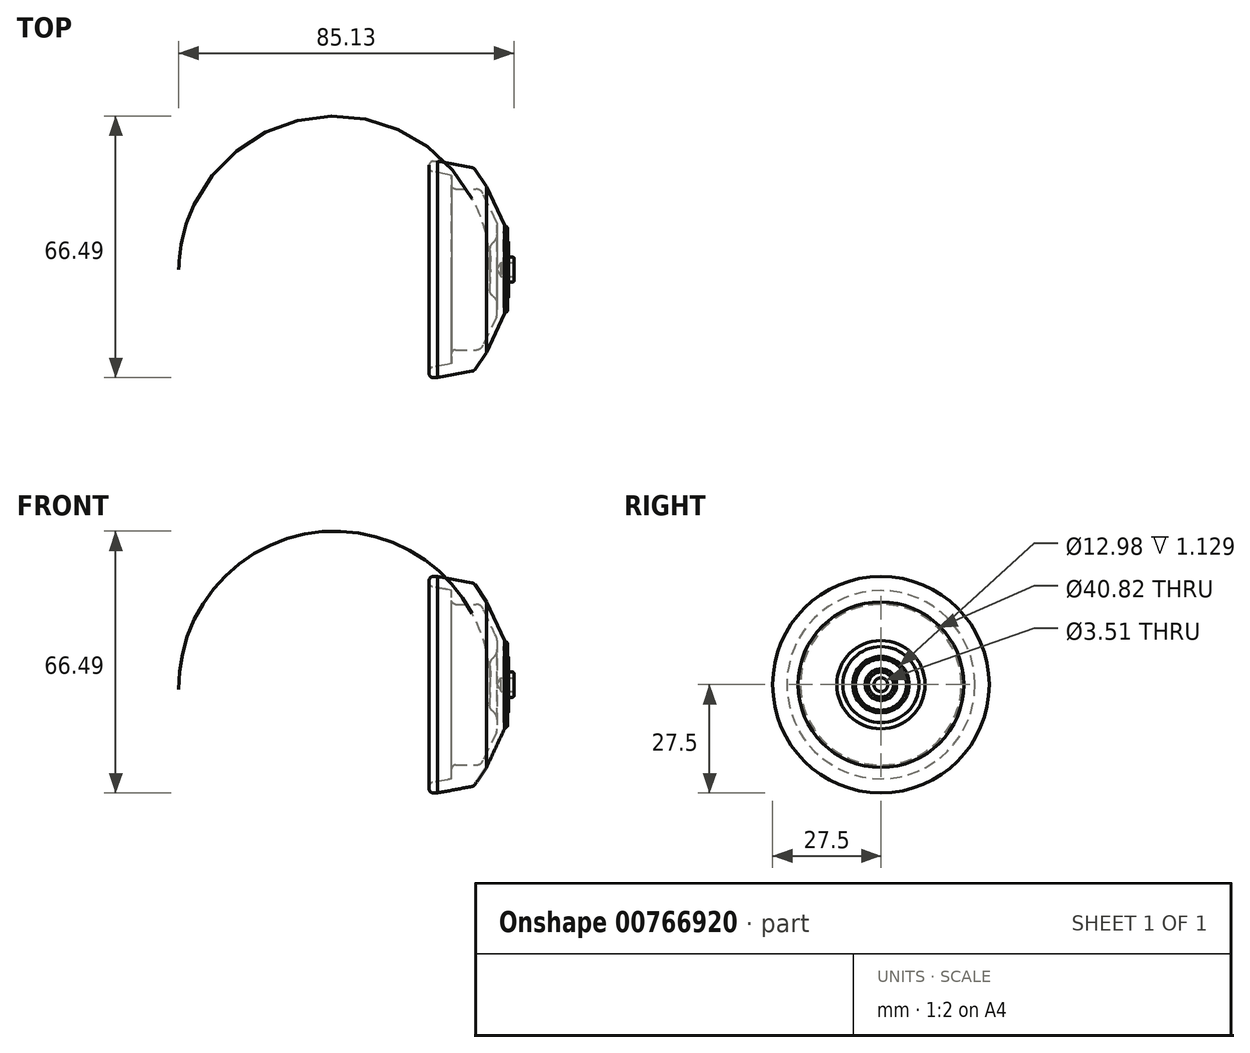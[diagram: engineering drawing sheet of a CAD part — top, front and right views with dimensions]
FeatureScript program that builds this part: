
annotation { "Feature Type Name" : "Feature", "Feature Type Description" : "" }
export const myFeature = defineFeature(function(context is Context, id is Id, definition is map)
    precondition{}
    {
        {
            var Q0;
            Q0=qCreatedBy(makeId("Front.planeOp"),FACE);
            var sketch = newSketch(context, id + "F0", { "sketchPlane" : qUnion([Q0])});
            skLineSegment(sketch, "E0", {"start": v(4.25, 1.75) * mm, "end": v(1.05, 1.75) * mm});
            skArc(sketch, "E1", {"start": v(2.42, 9.65) * mm, "mid": v(2.6, 9.73) * mm, "end": v(2.67, 9.9) * mm});
            skLineSegment(sketch, "E2", {"start": v(1.67, 7.15) * mm, "end": v(1.67, 9.65) * mm});
            skLineSegment(sketch, "E3", {"start": v(1.67, 9.65) * mm, "end": v(2.42, 9.65) * mm});
            skLineSegment(sketch, "E4", {"start": v(2.93, 6.62) * mm, "end": v(2.93, 6.9) * mm});
            skLineSegment(sketch, "E5", {"start": v(1.05, 1.75) * mm, "end": v(0, 0) * mm});
            skArc(sketch, "E6", {"start": v(2.93, 6.9) * mm, "mid": v(2.85, 7.08) * mm, "end": v(2.67, 7.15) * mm});
            skArc(sketch, "E7", {"start": v(2.8, 6.5) * mm, "mid": v(2.9, 6.53) * mm, "end": v(2.93, 6.62) * mm});
            skLineSegment(sketch, "E8", {"start": v(1.67, 6.5) * mm, "end": v(2.8, 6.5) * mm});
            skLineSegment(sketch, "E9", {"start": v(1.67, 4) * mm, "end": v(1.67, 6.5) * mm});
            skLineSegment(sketch, "E10", {"start": v(1.67, 4) * mm, "end": v(2.37, 4) * mm});
            skLineSegment(sketch, "E11", {"start": v(4.25, 1.75) * mm, "end": v(4.25, 2.97) * mm});
            skLineSegment(sketch, "E12", {"start": v(2.37, 3.19) * mm, "end": v(2.37, 4) * mm});
            skLineSegment(sketch, "E13", {"start": v(4.16, 3.09) * mm, "end": v(3.88, 3.18) * mm});
            skLineSegment(sketch, "E14", {"start": v(2.37, 3.19) * mm, "end": v(3.84, 3.19) * mm});
            skLineSegment(sketch, "E15", {"start": v(1.67, 7.15) * mm, "end": v(2.67, 7.15) * mm});
            skArc(sketch, "E16", {"start": v(4.25, 2.97) * mm, "mid": v(4.22, 3.04) * mm, "end": v(4.16, 3.09) * mm});
            skArc(sketch, "E17", {"start": v(3.88, 3.18) * mm, "mid": v(3.86, 3.18) * mm, "end": v(3.84, 3.19) * mm});
            skLineSegment(sketch, "E18", {"start": v(4.75, 1) * mm, "end": v(4.75, 2.5) * mm});
            skPoint(sketch, "E19.orphan", {"position": v(4.75, 0) * mm});
            skPoint(sketch, "E20.end.orphan", {"position": v(-17.25, -3.5) * mm});
            skPoint(sketch, "E20.start.orphan", {"position": v(4.75, -3.5) * mm});
            skLineSegment(sketch, "E21", {"start": v(-17.25, 27.5) * mm, "end": v(-15.16, 27.5) * mm});
            skLineSegment(sketch, "E22", {"start": v(2.67, 9.9) * mm, "end": v(2.67, 10.56) * mm});
            skLineSegment(sketch, "E23", {"start": v(2.67, 10.56) * mm, "end": v(1.87, 11.22) * mm});
            skLineSegment(sketch, "E24", {"start": v(1.87, 11.22) * mm, "end": v(-2.73, 21.05) * mm});
            skLineSegment(sketch, "E25", {"start": v(-2.73, 21.05) * mm, "end": v(-5.9, 25.79) * mm});
            skLineSegment(sketch, "E26", {"start": v(-5.9, 25.79) * mm, "end": v(-15.16, 27.5) * mm});
            skPoint(sketch, "E27.start.orphan", {"position": v(-17.25, 0) * mm});
            skLineSegment(sketch, "E28.0", {"start": v(0, 11.68) * mm, "end": v(-4.1, 20.4) * mm});
            skPoint(sketch, "E29.endSnap0", {"position": v(-10.53, 26.64) * mm});
            skLineSegment(sketch, "E30", {"start": v(-10.53, 20.4) * mm, "end": v(-4.1, 20.4) * mm});
            skPoint(sketch, "E31.orphan", {"position": v(-6.18, 24.31) * mm});
            skLineSegment(sketch, "E32", {"start": v(-17.25, 26.03) * mm, "end": v(-17.25, 27.5) * mm});
            skLineSegment(sketch, "E33", {"start": v(0, 0) * mm, "end": v(-1.64, 0) * mm});
            skLineSegment(sketch, "E34", {"start": v(0, 11.68) * mm, "end": v(0, 8.89) * mm});
            skArc(sketch, "E35", {"start": v(-2.04, 6.32) * mm, "mid": v(-0.57, 7.25) * mm, "end": v(0, 8.89) * mm});
            skArc(sketch, "E36", {"start": v(-1.64, 0) * mm, "mid": v(-1.71, 3.17) * mm, "end": v(-2.04, 6.32) * mm});
            skPoint(sketch, "E37.oppositeSnap0", {"position": v(-10.67, 22.79) * mm});
            skLineSegment(sketch, "E37.bottom", {"start": v(-10.53, 20.4) * mm, "end": v(-11.57, 20.4) * mm});
            skPoint(sketch, "E38.orphan", {"position": v(-10.8, 25.17) * mm});
            skLineSegment(sketch, "E39", {"start": v(-17.25, 26.03) * mm, "end": v(-17.25, 25.02) * mm});
            skLineSegment(sketch, "E40", {"start": v(-17.25, 25.02) * mm, "end": v(-12.6, 24.16) * mm});
            skPoint(sketch, "E41.0.end.orphan", {"position": v(-15.43, 26.03) * mm});
            skLineSegment(sketch, "E42", {"start": v(-11.57, 20.4) * mm, "end": v(-11.57, 23.9) * mm});
            skPoint(sketch, "E42.endSnap0", {"position": v(-11.57, 20.4) * mm});
            skLineSegment(sketch, "E43", {"start": v(-11.57, 23.9) * mm, "end": v(-12.6, 24.16) * mm});
            skPoint(sketch, "E37.right.end.orphan", {"position": v(-12.6, 22.79) * mm});
            skPoint(sketch, "E37.right.start.orphan", {"position": v(-12.6, 20.4) * mm});
            skSolve(sketch);
        }
        {
            var Q0;
            Q0=makeQuery(id+"F0.imprint","IMPRINT",FACE,{"disambiguationData":[TD([[makeQuery(id+"F0.imprint","IMPRINT",EDGE,{"derivedFrom":sQuery(id+"F0.wireOp",EDGE,"E0")}),-1.0]])]});
            var Q1;
            Q1=sQuery(id+"F0.wireOp",EDGE,"E33");
            revolve(context, id + "F1", {"surfaceOperationType" : NewSurfaceOperationType.NEW, "entities" : qUnion([Q0]), "axis" : qUnion([Q1]), "revolveType" : RevolveType.FULL});
        }
        {
            var Q0;
            Q0=makeQuery(id+"F1.opRevolve","SWEPT_EDGE",EDGE,{"disambiguationData":[OSD([sQuery(id+"F0.wireOp",EDGE,"E21"),sQuery(id+"F0.wireOp",EDGE,"E32")])]});
            var Q1;
            Q1=makeQuery(id+"F1.opRevolve","SWEPT_EDGE",EDGE,{"disambiguationData":[OSD([sQuery(id+"F0.wireOp",EDGE,"E39"),sQuery(id+"F0.wireOp",EDGE,"E40")])]});
            fillet(context, id + "F2", {"entities" : qUnion([Q0, Q1]), "radius" : 1 * mm, "tangentPropagation" : true, "allowEdgeOverflow" : false});
        }
        {
            var Q0;
            Q0=makeQuery(id+"F1.opRevolve","SWEPT_EDGE",EDGE,{"disambiguationData":[OSD([sQuery(id+"F0.wireOp",EDGE,"E22"),sQuery(id+"F0.wireOp",EDGE,"E23")])]});
            fillet(context, id + "F3", {"entities" : qUnion([Q0]), "radius" : .5 * mm, "tangentPropagation" : true, "allowEdgeOverflow" : false});
        }
        {
            var Q0;
            Q0=makeQuery(id+"F1.opRevolve","SWEPT_EDGE",EDGE,{"disambiguationData":[OSD([sQuery(id+"F0.wireOp",EDGE,"E25"),sQuery(id+"F0.wireOp",EDGE,"E26")])]});
            fillet(context, id + "F4", {"entities" : qUnion([Q0]), "radius" : 1 * mm, "tangentPropagation" : true, "allowEdgeOverflow" : false});
        }
        {
            var Q0;
            Q0=makeQuery(id+"F1.opRevolve","SWEPT_EDGE",EDGE,{"disambiguationData":[OSD([sQuery(id+"F0.wireOp",EDGE,"E37.bottom"),sQuery(id+"F0.wireOp",EDGE,"E37.right")])]});
            var Q1;
            Q1=makeQuery(id+"F1.opRevolve","SWEPT_EDGE",EDGE,{"disambiguationData":[OSD([sQuery(id+"F0.wireOp",EDGE,"YovRWjks-4oVz-m1WY-QORR-ZGdhdRptP0TG"),sQuery(id+"F0.wireOp",EDGE,"E40")])]});
            fillet(context, id + "F5", {"entities" : qUnion([Q0, Q1]), "radius" : 1 * mm, "tangentPropagation" : true, "allowEdgeOverflow" : false});
        }
        {
            var Q0;
            Q0=makeQuery(id+"F1.opRevolve","SWEPT_EDGE",EDGE,{"disambiguationData":[OSD([sQuery(id+"F0.wireOp",EDGE,"E28.0"),sQuery(id+"F0.wireOp",EDGE,"E30")])]});
            var Q1;
            Q1=makeQuery(id+"F1.opRevolve","SWEPT_EDGE",EDGE,{"disambiguationData":[OSD([sQuery(id+"F0.wireOp",EDGE,"E28.0"),sQuery(id+"F0.wireOp",EDGE,"E34")])]});
            fillet(context, id + "F6", {"entities" : qUnion([Q0, Q1]), "radius" : 2 * mm, "tangentPropagation" : true, "allowEdgeOverflow" : false});
        }
        {
            var Q0;
            Q0=makeQuery(id+"F1.opRevolve","SWEPT_EDGE",EDGE,{"disambiguationData":[OSD([sQuery(id+"F0.wireOp",EDGE,"E35"),sQuery(id+"F0.wireOp",EDGE,"E36")])]});
            fillet(context, id + "F7", {"entities" : qUnion([Q0]), "radius" : 2 * mm, "tangentPropagation" : true, "allowEdgeOverflow" : false});
        }
    });
